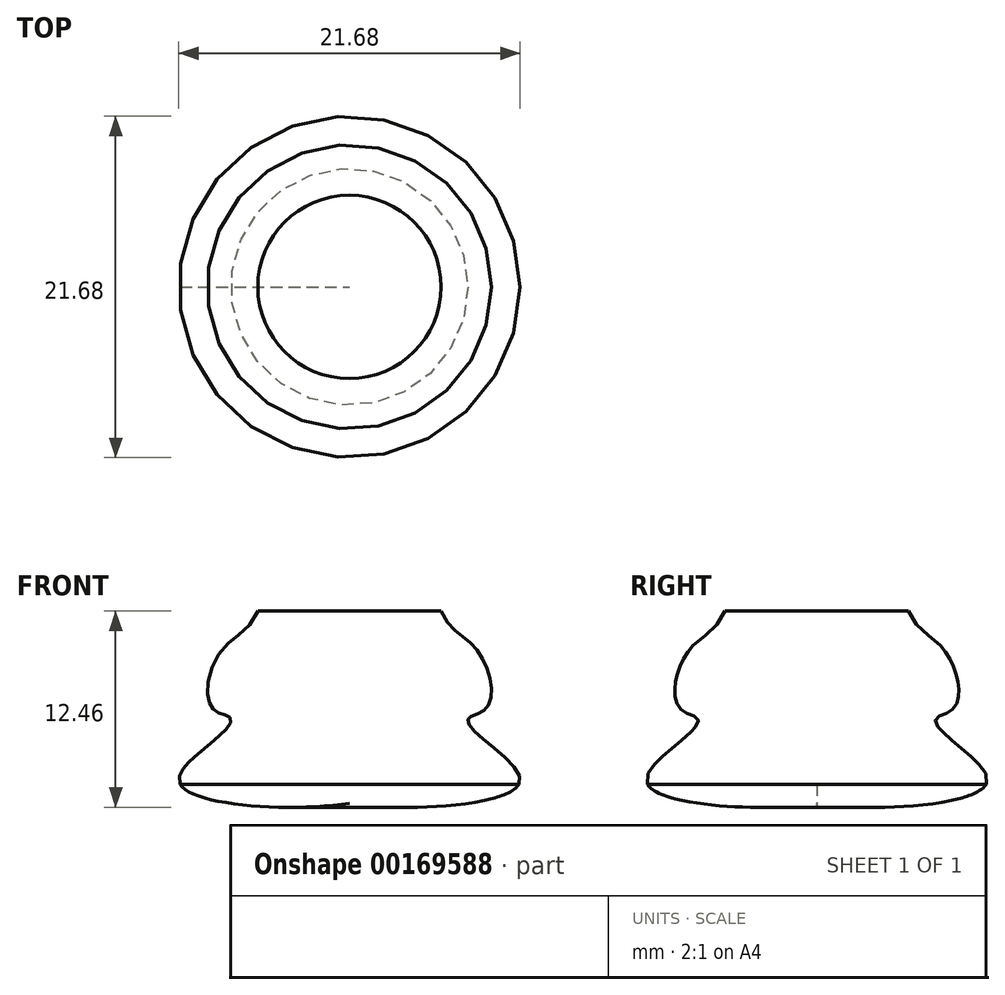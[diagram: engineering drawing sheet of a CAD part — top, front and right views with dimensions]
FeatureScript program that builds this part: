
annotation { "Feature Type Name" : "Feature", "Feature Type Description" : "" }
export const myFeature = defineFeature(function(context is Context, id is Id, definition is map)
    precondition{}
    {
        {
            var Q0;
            Q0=qCreatedBy(makeId("Front.planeOp"),FACE);
            var sketch = newSketch(context, id + "F0", { "sketchPlane" : qUnion([Q0])});
            skPoint(sketch, "E0.orphan", {"position": v(0, 46.2) * mm});
            skFitSpline(sketch, "E1", {"points": [v(-5, 38.2) * mm, v(-4.67, 23.97) * mm, v(-6.45, 21.68) * mm, v(-7.48, 19.59) * mm, v(-7.14, 18.15) * mm, v(-6.3, 17.73) * mm, v(-6.97, 16.71) * mm, v(-9, 14.3) * mm, v(0, 13.22) * mm], "startDerivative": vector(-4, -17.38) * mm, "endDerivative": vector(48.53, 7.54) * mm});
            skLineSegment(sketch, "E2", {"start": v(-8.97, 14.24) * mm, "end": v(0, 14.2) * mm});
            skLineSegment(sketch, "E3", {"start": v(0, 23.4) * mm, "end": v(0, 13.22) * mm});
            skPoint(sketch, "E4.orphan", {"position": v(216.1, 13.22) * mm});
            skLineSegment(sketch, "E5", {"start": v(-4.85, 23.4) * mm, "end": v(-0.19, 23.4) * mm});
            skPoint(sketch, "E6.bottom.end.orphan", {"position": v(-5, 46.2) * mm});
            skLineSegment(sketch, "E7", {"start": v(-0.93, 23.4) * mm, "end": v(0, 23.4) * mm});
            skSolve(sketch);
        }
        {
            var Q0;
            Q0=qCreatedBy(makeId("Front.planeOp"),FACE);
            var sketch = newSketch(context, id + "F1", { "sketchPlane" : qUnion([Q0])});
            skLineSegment(sketch, "E8", {"start": v(0, 42.86) * mm, "end": v(0, 13.5) * mm});
            skSolve(sketch);
        }
        {
            var Q0;
            Q0=qSketchRegion(id+"F0",true);
            var Q1;
            Q1=sQuery(id+"F1.wireOp",EDGE,"E8");
            revolve(context, id + "F2", {"entities" : qUnion([Q0]), "axis" : qUnion([Q1]), "revolveType" : RevolveType.FULL});
        }
        {
            var Q0;
            Q0=qCreatedBy(makeId("Front.planeOp"),FACE);
            var sketch = newSketch(context, id + "F3", { "sketchPlane" : qUnion([Q0])});
            skLineSegment(sketch, "E9", {"start": v(0, 50.19) * mm, "end": v(0, 0) * mm});
            skSolve(sketch);
        }
        {
            var Q0;
            Q0=makeQuery(id+"F2.opRevolve","SWEPT_BODY",BODY,{"disambiguationData":[OSD([sQuery(id+"F0.wireOp",EDGE,"E1"),sQuery(id+"F0.wireOp",EDGE,"E2"),sQuery(id+"F0.wireOp",EDGE,"E3"),sQuery(id+"F0.wireOp",EDGE,"E5"),sQuery(id+"F0.wireOp",EDGE,"E7")])]});
            var Q1;
            Q1=sQuery(id+"F3.wireOp",VERTEX,"E9.end");
            var Q2;
            Q2=sQuery(id+"F3.wireOp",VERTEX,"E9.end");
            transform(context, id + "F4", {"entities" : qUnion([Q0]), "transformType" : TransformType.SCALE_UNIFORMLY, "scale" : 1.2, "scalePoint" : qUnion([Q2]), "makeCopy" : false});
        }
    });
